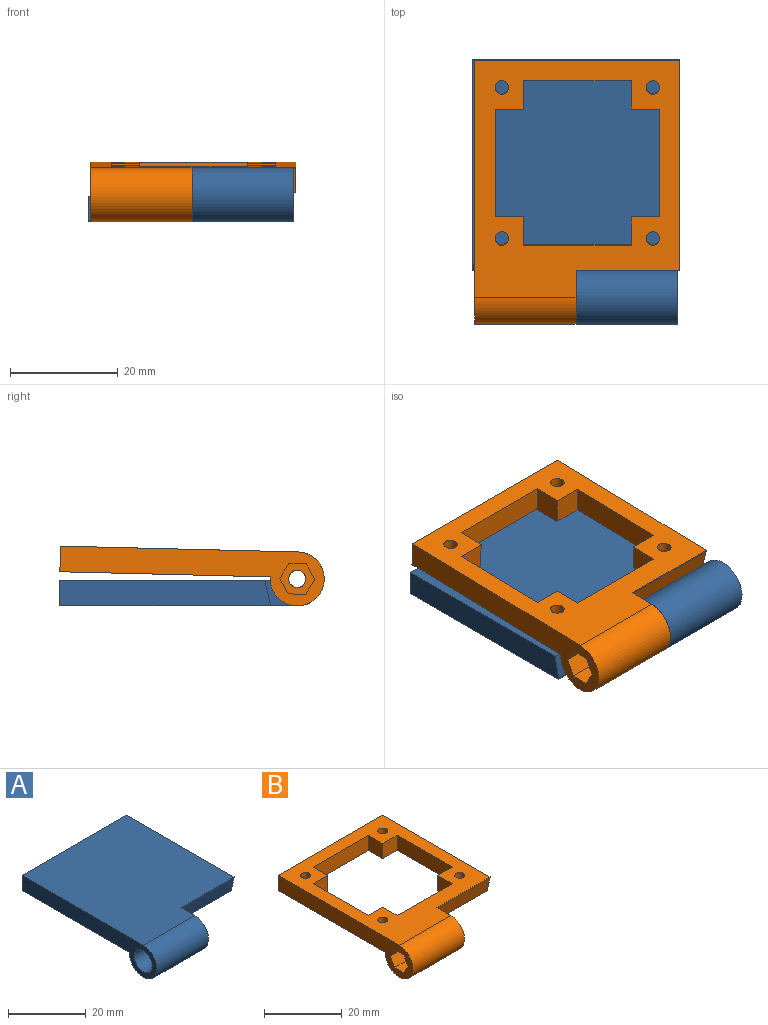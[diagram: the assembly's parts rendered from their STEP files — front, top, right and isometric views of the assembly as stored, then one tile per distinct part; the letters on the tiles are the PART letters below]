
ASSEMBLY  parts=2 mates=1
PART A: 13 faces, bbox 38x49x10 mm
  f0: plane 19.25x0.25mm, normal (0,-1,0), area 4.8mm2, adj f3,f4,f7,f12
  f1: plane 49x10mm, normal (-1,0,0), area 236mm2, adj f3,f5,f6,f8,f10,f11
  f2: cylinder r=1.6mm len=13.75mm, axis (1,0,0), area 138.2mm2, adj f7,f9
  f3: plane 44x38mm, normal (0,0,1), area 1575.8mm2, adj f0,f1,f4,f5,f6,f7
  f4: plane 39x4.75mm, normal (1,0,0), area 183mm2, adj f0,f3,f5,f11,f12
  f5: plane 38x4.75mm, normal (0,1,0), area 180.5mm2, adj f1,f3,f4,f11
  f6: cylinder r=5mm len=18.75mm, axis (-1,0,0), area 441.8mm2, adj f1,f3,f7,f10
  f7: plane 11x10mm, normal (1,0,0), area 78.1mm2, adj f0,f2,f3,f6,f10,f11,f12
  f8: cylinder r=3.25mm len=6.5mm, axis (-1,0,0), area 102.1mm2, adj f1,f9
  f9: plane 6.5x6.5mm, normal (-1,0,0), area 25.1mm2, adj f2,f8
  f10: plane 18.75x0.25mm, normal (0,1,0), area 4.7mm2, adj f1,f6,f7,f11
  f11: plane 39x38mm, normal (0,0,-1), area 1462.7mm2, adj f1,f4,f5,f7,f10,f12
  f12: plane 19.25x4.5mm, normal (0,-0.98,-0.22), area 88.7mm2, adj f0,f4,f7,f11
PART B: 34 faces, bbox 38x49x10 mm
  f0: plane 19.25x0.25mm, normal (0,-1,0), area 4.8mm2, adj f3,f4,f19,f33
  f1: plane 49x10mm, normal (-1,0,0), area 241.7mm2, adj f3,f5,f18,f24,f25,f26,f27,f28
  f2: cylinder r=1.6mm len=13.75mm, axis (1,0,0), area 138.2mm2, adj f19,f30
  f3: plane 44x38mm, normal (0,0,1), area 736.1mm2, adj f0,f1,f4,f5,f6,f7,f8,f9
  f4: plane 39x4.75mm, normal (1,0,0), area 183mm2, adj f0,f3,f5,f32,f33
  f5: plane 38x4.75mm, normal (0,1,0), area 180.5mm2, adj f1,f3,f4,f32
  f6: plane 5.25x4.75mm, normal (0,1,0), area 24.9mm2, adj f3,f16,f22,f32
  f7: plane 5.25x4.75mm, normal (0,-1,0), area 24.9mm2, adj f3,f8,f22,f32
  f8: plane 5.25x4.75mm, normal (1,0,0), area 24.9mm2, adj f3,f7,f21,f32
  f9: plane 5.25x4.75mm, normal (-1,0,0), area 24.9mm2, adj f3,f10,f21,f32
  f10: plane 5.25x4.75mm, normal (0,-1,0), area 24.9mm2, adj f3,f9,f20,f32
  f11: plane 5.25x4.75mm, normal (0,1,0), area 24.9mm2, adj f3,f12,f20,f32
  f12: plane 5.25x4.75mm, normal (-1,0,0), area 24.9mm2, adj f3,f11,f23,f32
  f13: cylinder r=1.25mm len=4.75mm, axis (0,0,-1), area 37.3mm2, adj f3,f32
  f14: cylinder r=1.25mm len=4.75mm, axis (0,0,-1), area 37.3mm2, adj f3,f32
  f15: cylinder r=1.25mm len=4.75mm, axis (0,0,-1), area 37.3mm2, adj f3,f32
  f16: plane 5.25x4.75mm, normal (1,0,0), area 24.9mm2, adj f3,f6,f23,f32
  f17: cylinder r=1.25mm len=4.75mm, axis (0,0,-1), area 37.3mm2, adj f3,f32
  f18: cylinder r=5mm len=18.75mm, axis (-1,0,0), area 441.8mm2, adj f1,f3,f19,f31
  f19: plane 11x10mm, normal (1,0,0), area 78.1mm2, adj f0,f2,f3,f18,f31,f32,f33
  f20: plane 20x4.75mm, normal (-1,0,0), area 95mm2, adj f3,f10,f11,f32
  f21: plane 20x4.75mm, normal (0,-1,0), area 95mm2, adj f3,f8,f9,f32
  f22: plane 20x4.75mm, normal (1,0,0), area 95mm2, adj f3,f6,f7,f32
  f23: plane 20x4.75mm, normal (0,1,0), area 95mm2, adj f3,f12,f16,f32
  f24: plane 5x2.81mm, normal (0,-0.87,0.5), area 16.3mm2, adj f1,f25,f29,f30
  f25: plane 5x3.25mm, normal (0,0,1), area 16.3mm2, adj f1,f24,f26,f30
  f26: plane 5x2.81mm, normal (0,0.87,0.5), area 16.3mm2, adj f1,f25,f27,f30
  f27: plane 5x2.81mm, normal (0,0.87,-0.5), area 16.3mm2, adj f1,f26,f28,f30
  f28: plane 5x3.25mm, normal (0,0,-1), area 16.3mm2, adj f1,f27,f29,f30
  f29: plane 5x2.81mm, normal (0,-0.87,-0.5), area 16.3mm2, adj f1,f24,f28,f30
  f30: plane 6.5x5.63mm, normal (-1,0,0), area 19.4mm2, adj f2,f24,f25,f26,f27,f28,f29
  f31: plane 18.75x0.25mm, normal (0,1,0), area 4.7mm2, adj f1,f18,f19,f32
  f32: plane 39x38mm, normal (0,0,-1), area 623.1mm2, adj f1,f4,f5,f6,f7,f8,f9,f10
  f33: plane 19.25x4.5mm, normal (0,-0.98,-0.22), area 88.7mm2, adj f0,f4,f19,f32
PLACE A rot(axis=(0,1,0),180deg) t=(50.07,6.36,-17.4)mm fixed
PLACE B rot(axis=(1,0,0),1.4deg) t=(50.57,6.35,-16.78)mm
MATE revolute A.f2 <-> B.f2  axis (-1,0,0) through (20.32,-18.64,-17.4)mm
